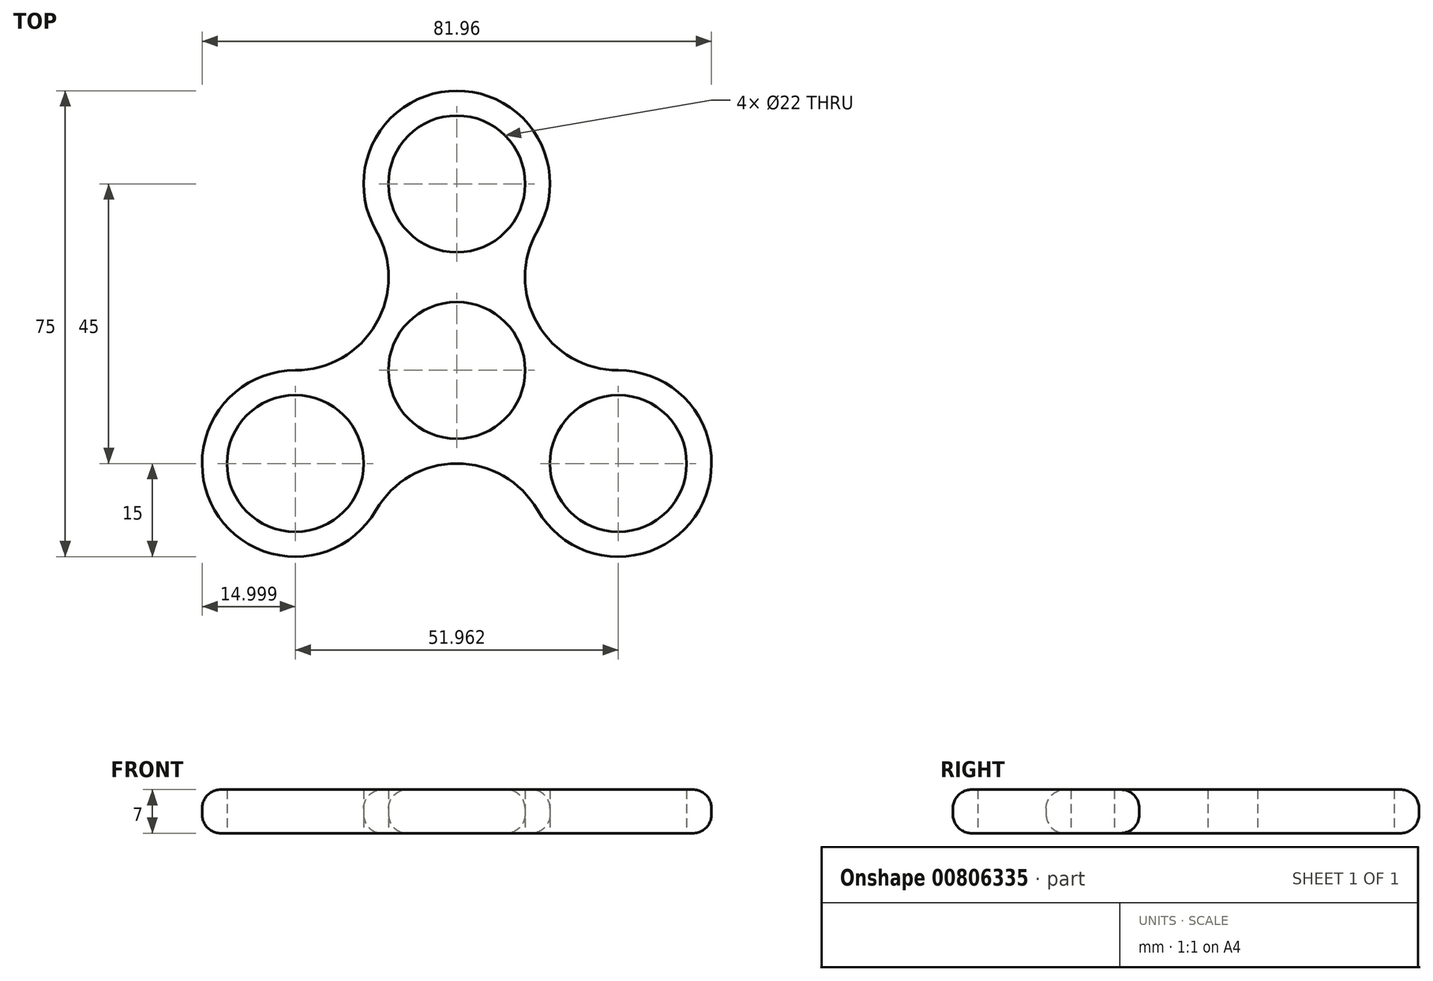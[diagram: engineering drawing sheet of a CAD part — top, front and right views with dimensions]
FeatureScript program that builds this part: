
annotation { "Feature Type Name" : "Feature", "Feature Type Description" : "" }
export const myFeature = defineFeature(function(context is Context, id is Id, definition is map)
    precondition{}
    {
        {
            var Q0;
            Q0=qCreatedBy(makeId("Top.planeOp"),FACE);
            var sketch = newSketch(context, id + "F0", { "sketchPlane" : qUnion([Q0])});
            skCircle(sketch, "E0", {"center": v(0, 0) * mm, "radius": 11 * mm});
            skCircle(sketch, "E1", {"center": v(0, 0) * mm, "radius": 15 * mm});
            skCircle(sketch, "E2", {"center": v(0, 30) * mm, "radius": 11 * mm});
            skCircle(sketch, "E3", {"center": v(0, 30) * mm, "radius": 15 * mm});
            skPoint(sketch, "E4.center", {"position": v(0, 0.5) * mm});
            skArc(sketch, "E5.1.0", {"start": v(-25.98, 0) * mm, "mid": v(-13, 7.5) * mm, "end": v(-13, 22.5) * mm});
            skCircle(sketch, "E5.2.0", {"center": v(-25.98, -15) * mm, "radius": 15 * mm});
            skCircle(sketch, "E5.2.1", {"center": v(-25.98, -15) * mm, "radius": 11 * mm});
            skArc(sketch, "E5.3.0", {"start": v(13, -22.5) * mm, "mid": v(0, -15) * mm, "end": v(-13, -22.5) * mm});
            skCircle(sketch, "E5.4.0", {"center": v(25.98, -15) * mm, "radius": 15 * mm});
            skCircle(sketch, "E5.4.1", {"center": v(25.98, -15) * mm, "radius": 11 * mm});
            skArc(sketch, "E5.5.0", {"start": v(13, 22.5) * mm, "mid": v(13, 7.5) * mm, "end": v(25.98, 0) * mm});
            skSolve(sketch);
        }
        {
            var Q0;
            Q0=makeQuery(id+"F0.imprint","IMPRINT",FACE,{"disambiguationData":[TD([[makeQuery(id+"F0.imprint","IMPRINT",EDGE,{"derivedFrom":sQuery(id+"F0.wireOp",EDGE,"E1")}),-1.0]])]});
            var Q1;
            Q1=makeQuery(id+"F0.imprint","IMPRINT",FACE,{"disambiguationData":[TD([[makeQuery(id+"F0.imprint","IMPRINT",EDGE,{"derivedFrom":sQuery(id+"F0.wireOp",EDGE,"c202e4ac-ae93-4b29-baa2-4fd0cf997ff0.1.0")}),-1.0]])]});
            var Q2;
            Q2=makeQuery(id+"F0.imprint","IMPRINT",FACE,{"disambiguationData":[TD([[makeQuery(id+"F0.imprint","IMPRINT",EDGE,{"derivedFrom":sQuery(id+"F0.wireOp",EDGE,"E0")}),-1.0]])]});
            var Q3;
            Q3=makeQuery(id+"F0.imprint","IMPRINT",FACE,{"disambiguationData":[TD([[makeQuery(id+"F0.imprint","IMPRINT",EDGE,{"derivedFrom":sQuery(id+"F0.wireOp",EDGE,"E2")}),-1.0]])]});
            var Q4;
            Q4=makeQuery(id+"F0.imprint","IMPRINT",FACE,{"disambiguationData":[TD([[makeQuery(id+"F0.imprint","IMPRINT",EDGE,{"derivedFrom":sQuery(id+"F0.wireOp",EDGE,"c202e4ac-ae93-4b29-baa2-4fd0cf997ff0.2.0")}),-1.0]])]});
            var Q5;
            Q5=makeQuery(id+"F0.imprint","IMPRINT",FACE,{"disambiguationData":[TD([[makeQuery(id+"F0.imprint","IMPRINT",EDGE,{"derivedFrom":sQuery(id+"F0.wireOp",EDGE,"0e0c9052-6751-44d5-bc73-aae295e7aca2.2.0")}),-1.0]])]});
            var Q6;
            Q6=makeQuery(id+"F0.imprint","IMPRINT",FACE,{"disambiguationData":[TD([[makeQuery(id+"F0.imprint","IMPRINT",EDGE,{"derivedFrom":sQuery(id+"F0.wireOp",EDGE,"0e0c9052-6751-44d5-bc73-aae295e7aca2.4.0")}),-1.0]])]});
            var Q7;
            Q7=makeQuery(id+"F0.imprint","IMPRINT",FACE,{"disambiguationData":[TD([[makeQuery(id+"F0.imprint","IMPRINT",EDGE,{"derivedFrom":sQuery(id+"F0.wireOp",EDGE,"6d77e2d1-ec52-477d-ae8a-bde1fbb15b47.4.1")}),-1.0]])]});
            var Q8;
            Q8=makeQuery(id+"F0.imprint","IMPRINT",FACE,{"disambiguationData":[TD([[makeQuery(id+"F0.imprint","IMPRINT",EDGE,{"derivedFrom":sQuery(id+"F0.wireOp",EDGE,"6d77e2d1-ec52-477d-ae8a-bde1fbb15b47.2.1")}),-1.0]])]});
            var Q9;
            Q9=makeQuery(id+"F0.imprint","IMPRINT",FACE,{"disambiguationData":[TD([[makeQuery(id+"F0.imprint","IMPRINT",EDGE,{"derivedFrom":sQuery(id+"F0.wireOp",EDGE,"E5.4.1")}),-1.0]])]});
            var Q10;
            Q10=makeQuery(id+"F0.imprint","IMPRINT",FACE,{"disambiguationData":[TD([[makeQuery(id+"F0.imprint","IMPRINT",EDGE,{"derivedFrom":sQuery(id+"F0.wireOp",EDGE,"E5.2.1")}),-1.0]])]});
            extrude(context, id + "F1", {"entities" : qUnion([Q0, Q1, Q2, Q3, Q4, Q5, Q6, Q7, Q8, Q9, Q10]), "endBound" : BoundingType.SYMMETRIC, "depth" : 7 * mm, "offsetDistance" : 25.4 * mm});
        }
        {
            var Q0;
            Q0=makeQuery(id+"F1.opExtrude","CAP_EDGE",EDGE,{"disambiguationData":[OSD([sQuery(id+"F0.wireOp",EDGE,"E5.4.0")])],"isStart":false});
            fillet(context, id + "F2", {"entities" : qUnion([Q0]), "radius" : 3 * mm, "tangentPropagation" : true, "allowEdgeOverflow" : false});
        }
        {
            var Q0;
            Q0=makeQuery(id+"F1.opExtrude","CAP_EDGE",EDGE,{"disambiguationData":[OSD([sQuery(id+"F0.wireOp",EDGE,"E5.3.0")])],"isStart":true});
            fillet(context, id + "F3", {"entities" : qUnion([Q0]), "radius" : 3 * mm, "tangentPropagation" : true, "allowEdgeOverflow" : false});
        }
    });
